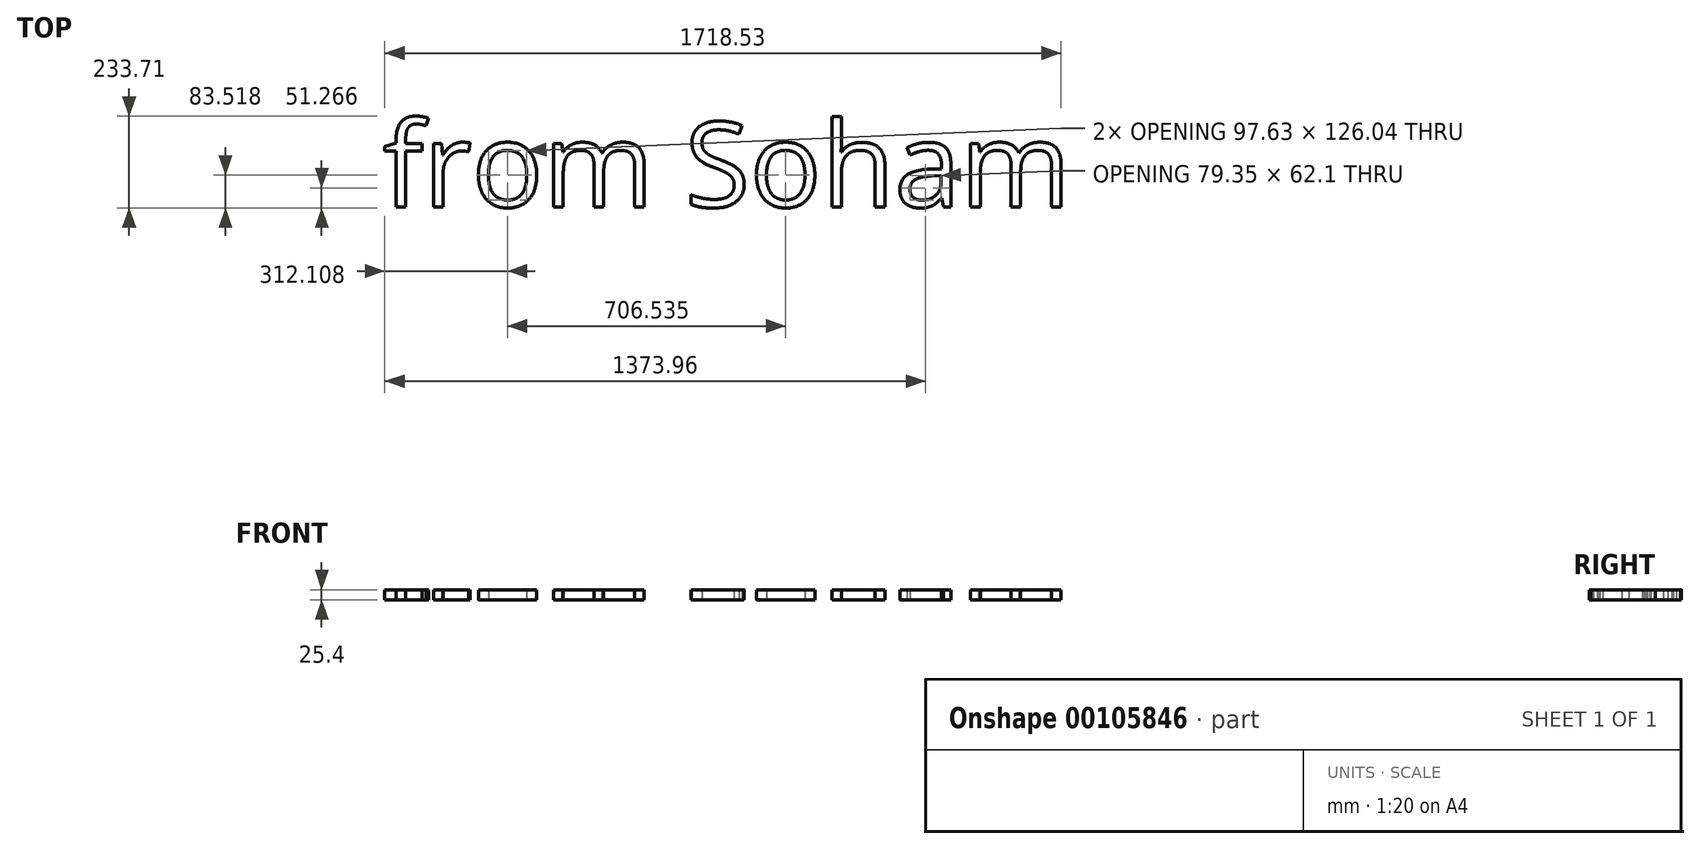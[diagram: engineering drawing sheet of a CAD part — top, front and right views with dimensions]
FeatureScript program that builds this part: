
annotation { "Feature Type Name" : "Feature", "Feature Type Description" : "" }
export const myFeature = defineFeature(function(context is Context, id is Id, definition is map)
    precondition{}
    {
        {
            var Q0;
            Q0=qCreatedBy(makeId("Top.planeOp"),FACE);
            var sketch = newSketch(context, id + "F0", { "sketchPlane" : qUnion([Q0])});
            skText(sketch, "E0", { "text": "from Soham", "fontName": "OpenSans-Regular.ttf"});
            const initialGuessFFtjWxOzJBpiXNFFi_24  = {"E0": [0.1174, -0.28135, 1, 0, 0.21712]};
            skSetInitialGuess(sketch, initialGuessFFtjWxOzJBpiXNFFi_24);
            skSolve(sketch);
        }
        {
            var Q0;
            Q0 = qSketchRegion(id + "F0", true);
            extrude(context, id + "F1", {"entities" : qUnion([Q0]), "depth" : 25.4 * mm});
        }
    });
